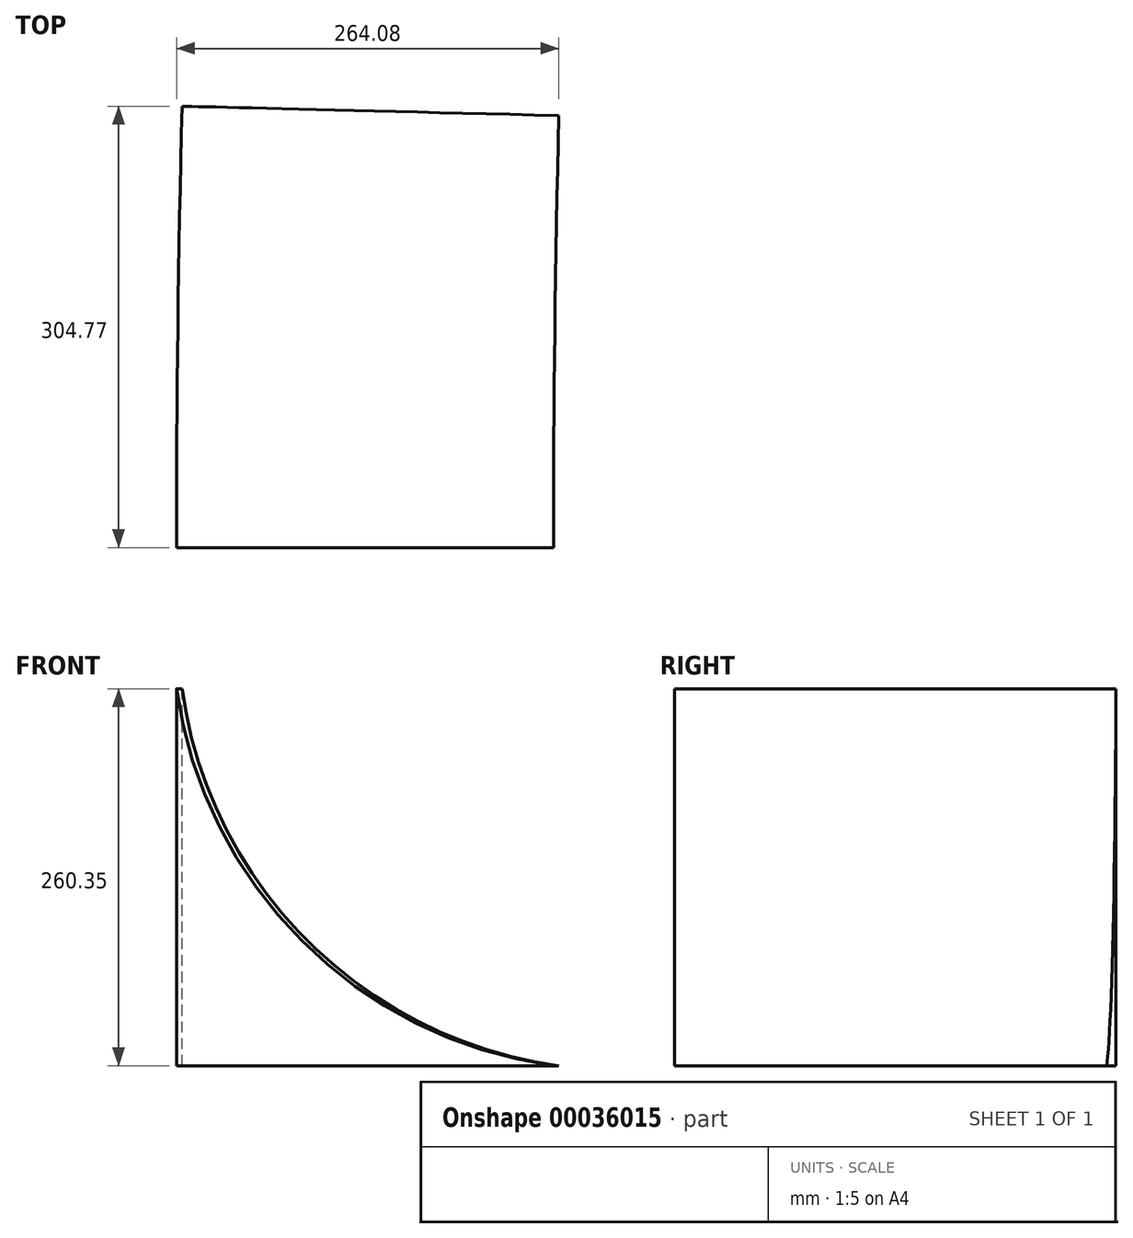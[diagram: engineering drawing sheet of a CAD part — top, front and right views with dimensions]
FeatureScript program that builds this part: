
annotation { "Feature Type Name" : "Feature", "Feature Type Description" : "" }
export const myFeature = defineFeature(function(context is Context, id is Id, definition is map)
    precondition{}
    {
        {
            var Q0;
            Q0=qCreatedBy(makeId("Front.planeOp"),FACE);
            var sketch = newSketch(context, id + "F0", { "sketchPlane" : qUnion([Q0])});
            skLineSegment(sketch, "E0", {"start": v(0, 0) * mm, "end": v(260.35, 0) * mm});
            skLineSegment(sketch, "E1", {"start": v(0, 0) * mm, "end": v(0, 260.35) * mm});
            skArc(sketch, "E2", {"start": v(0, 260.35) * mm, "mid": v(86.42, 86.42) * mm, "end": v(260.35, 0) * mm});
            skSolve(sketch);
        }
        {
            var Q0;
            Q0=qCreatedBy(makeId("Top.planeOp"),FACE);
            var sketch = newSketch(context, id + "F1", { "sketchPlane" : qUnion([Q0])});
            skArc(sketch, "E3", {"start": v(3.8, 304.77) * mm, "mid": v(0.95, 152.4) * mm, "end": v(0, 0) * mm});
            skLineSegment(sketch, "E4", {"start": v(12192, 0) * mm, "end": v(0, 0) * mm, "construction": true});
            skLineSegment(sketch, "E5", {"start": v(12192, 0) * mm, "end": v(3.8, 304.77) * mm, "construction": true});
            skSolve(sketch);
        }
        {
            var Q0;
            Q0=makeQuery(id+"F0.imprint","IMPRINT",FACE,{"disambiguationData":[TD([[makeQuery(id+"F0.imprint","IMPRINT",EDGE,{"derivedFrom":sQuery(id+"F0.wireOp",EDGE,"E0")}),1.0]])]});
            var Q1;
            Q1=sQuery(id+"F1.wireOp",EDGE,"E3");
            sweep(context, id + "F2", {"profiles" : qUnion([Q0]), "path" : qUnion([Q1])});
        }
    });
